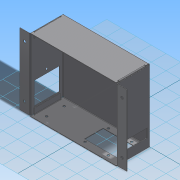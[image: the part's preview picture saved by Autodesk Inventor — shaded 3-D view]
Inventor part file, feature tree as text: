
AUTODESK INVENTOR PART (.ipt)
format: ipt  version: 2014 SP2 (Build 180246200, 246)  size: 437,248 bytes
history: native  units: in
note: dims shown in document units (in); Inventor stores cm internally (conversion verified against a paired STEP export)
features: other x10, sketch x7, sheet_metal_op x7, hole x4, projected_geometry x2, imported_body x1, plane x1, mirror x1
ambient origin geometry x8: Origin, YZ Plane, XZ Plane, XY Plane, X Axis, Y Axis, Z Axis, Center Point
bodies: Solid1 (feature_tree)
feature tree (33):
  imported_body  "Base"
  other  "Walls"
  other  "Tabs"
  sketch  "Sketch4"  dims[d10=0.128in d11=0.032in]
  hole  "Hole1"  [1 undecoded]
  hole  "Hole2"  [1 undecoded]
  hole  "Hole3"  [1 undecoded]
  sheet_metal_op  "Flange3"
  hole  "Hole4"  [1 undecoded]
  plane  "Work Plane1"
  mirror  "Mirror1"
  sketch  "Sketch1"  dims[d2=0.032in d3=0.032in]
  other  "Plate1"
  sketch  "Sketch2"  dims[d4=0.016in d5=0.064in]
  other  "Plate2"
  sheet_metal_op  "Bend1"
  sheet_metal_op  "Corner1"
  sketch  "Sketch3"  dims[d6=0.032in d8=90.0deg d9=0.032in]
  other  "Plate3"
  sheet_metal_op  "Bend2"
  sheet_metal_op  "Corner2"
  sketch  "Sketch5"  dims[d12=0.032in]
  other  "Plate4"
  sheet_metal_op  "Bend3"
  sheet_metal_op  "Corner3"
  sketch  "Sketch8"  dims[d13=0.032in]
  sketch  "Sketch9"  dims[d14=0.016in d15=0.064in d16=0.032in d17=0.4in d18=90.0deg d19=0.032in d20=0.128in d21=0.032in d22=0.032in d23=1.698in d24=1.814in d27=0.032in d28=0.0in d29=0.15in d30=0.75in d31=0.279in d32=0.25in d33=0.6871in d34=0.032in d35=0.8108in d36=0.032in d37=0.016in d38=0.064in d39=0.032in d40=0.7in d41=90.0deg d42=0.032in d43=0.128in d44=0.032in d45=0.032in d46=0.25in d47=0.25in d48=1.185in d50=0.15in d51=0.75in d52=0.375in d53=0.25in d54=0.5635in d55=0.032in d56=0.8108in d58=1.125in d59=0.1in d60=1.5748in d61=1.5748in d64=2.3622in d65=1.2598in d66=0.032in d67=0.0in d68=0.15in d69=0.75in d70=0.279in d71=0.25in d72=0.5635in d73=0.032in d74=0.8108in d75=0.1969in d76=1.8504in d77=0.5906in d78=0.5906in d79=0.032in d80=0.0in d81=1.75in d82=1.75in d83=1.75in d84=1.75in d85=1.125in d86=0.55in d88=0.2756in d89=0.7874in d90=0.4in d91=3.5in d92=0.177in d93=0.75in d94=0.332in d95=0.25in d96=0.5635in d97=0.032in d98=0.8108in]
  projected_geometry  "Projected Loop2"
  projected_geometry  "Projected Loop3"
  other  "Cut1"
  other  "Cut2"
  other  "Cut3"
  other  "Definition1"
note: 4 required parameter values undecoded (feature->parameter linkage not recoverable at this tier; creation-order binding heuristic only, values carry confidence <= 0.55)
